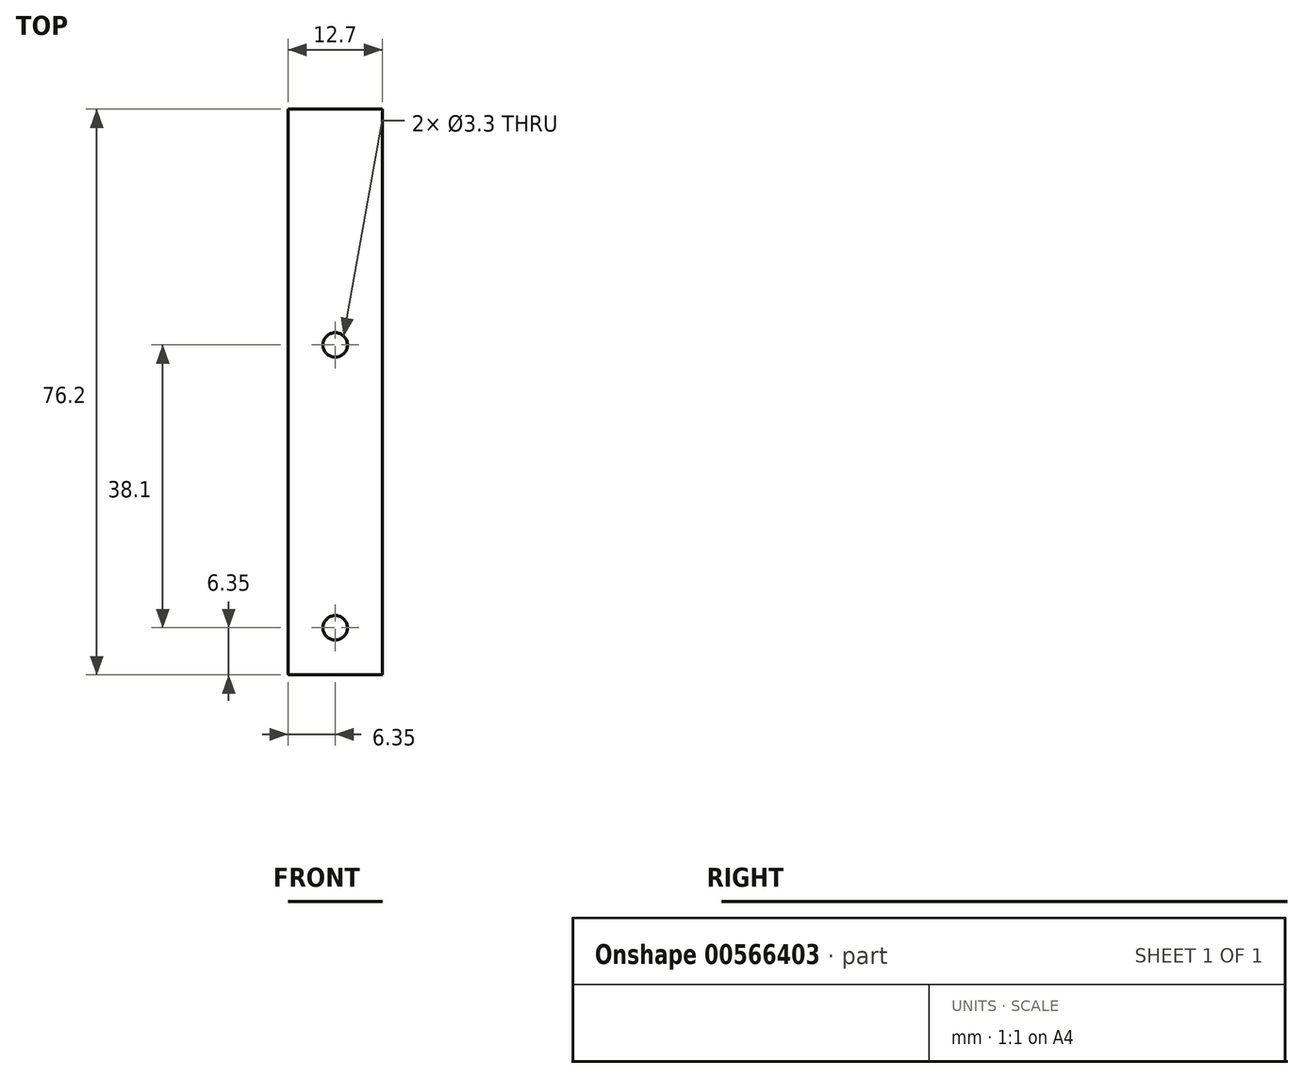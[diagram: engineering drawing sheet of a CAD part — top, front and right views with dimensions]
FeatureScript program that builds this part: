
annotation { "Feature Type Name" : "Feature", "Feature Type Description" : "" }
export const myFeature = defineFeature(function(context is Context, id is Id, definition is map)
    precondition{}
    {
        {
            var Q0;
            Q0=qCreatedBy(makeId("Top.planeOp"),FACE);
            var sketch = newSketch(context, id + "F0", { "sketchPlane" : qUnion([Q0])});
            skLineSegment(sketch, "E0.bottom", {"start": v(0, 0) * mm, "end": v(12.7, 0) * mm});
            skLineSegment(sketch, "E0.top", {"start": v(0, 76.2) * mm, "end": v(12.7, 76.2) * mm});
            skLineSegment(sketch, "E0.left", {"start": v(0, 0) * mm, "end": v(0, 76.2) * mm});
            skLineSegment(sketch, "E0.right", {"start": v(12.7, 0) * mm, "end": v(12.7, 76.2) * mm});
            skCircle(sketch, "E1", {"center": v(6.35, 6.35) * mm, "radius": 1.65 * mm});
            skPoint(sketch, "E1.centerSnap0", {"position": v(6.35, 0) * mm});
            skCircle(sketch, "E2", {"center": v(6.35, 44.45) * mm, "radius": 1.65 * mm});
            skPoint(sketch, "E2.centerSnap0", {"position": v(6.35, 76.2) * mm});
            skSolve(sketch);
        }
        {
            var Q0;
            Q0=makeQuery(id+"F0.imprint","IMPRINT",FACE,{"disambiguationData":[TD([[makeQuery(id+"F0.imprint","IMPRINT",EDGE,{"derivedFrom":sQuery(id+"F0.wireOp",EDGE,"E0.bottom")}),1.0]])]});
            extrude(context, id + "F1", {"entities" : qUnion([Q0]), "depth" : 1 / 203.2 * mm, "offsetDistance" : 25.4 * mm});
        }
    });
